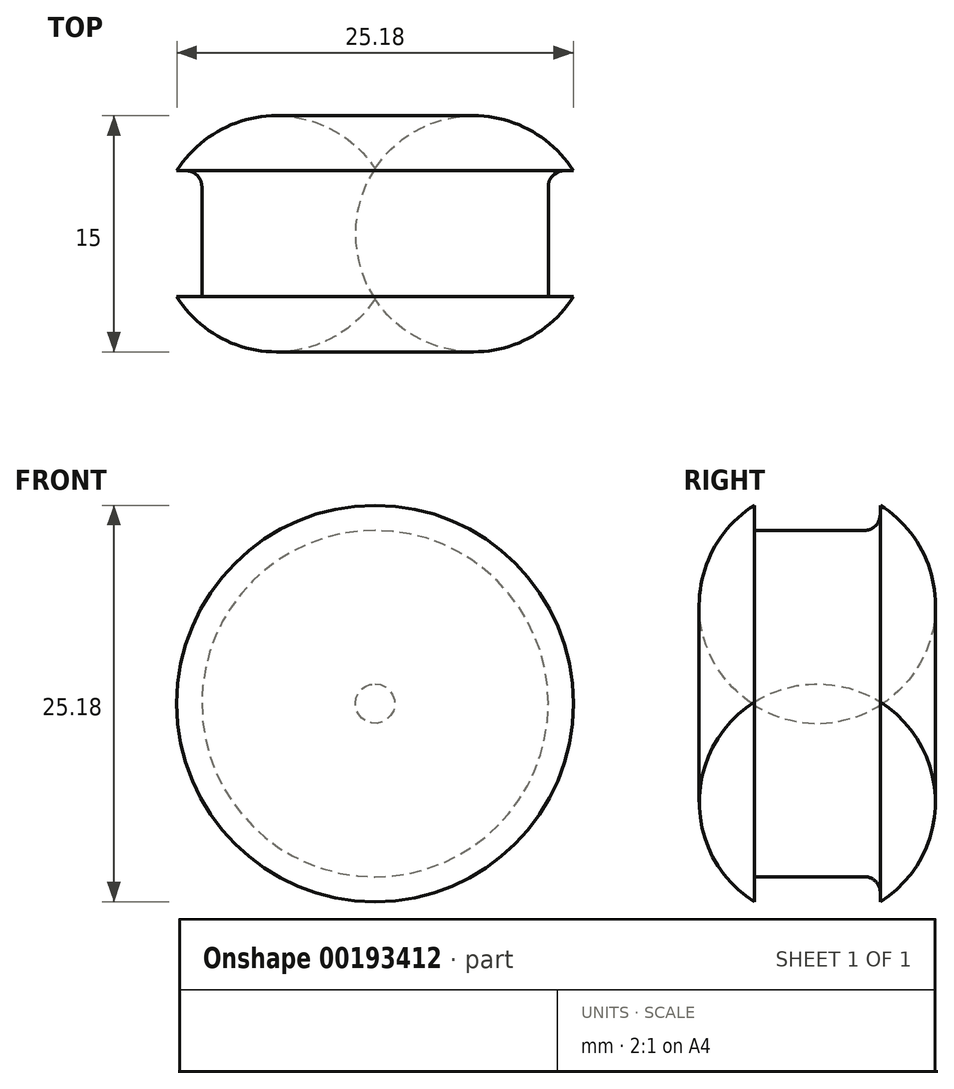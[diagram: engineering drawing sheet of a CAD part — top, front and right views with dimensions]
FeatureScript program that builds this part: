
annotation { "Feature Type Name" : "Feature", "Feature Type Description" : "" }
export const myFeature = defineFeature(function(context is Context, id is Id, definition is map)
    precondition{}
    {
        {
            var Q0;
            Q0=qCreatedBy(makeId("Right.planeOp"),FACE);
            var sketch = newSketch(context, id + "F0", { "sketchPlane" : qUnion([Q0])});
            skLineSegment(sketch, "E0", {"start": v(-28.73, 0) * mm, "end": v(29.21, 0) * mm, "construction": true});
            skLineSegment(sketch, "E1", {"start": v(-4, 11) * mm, "end": v(4, 11) * mm});
            skLineSegment(sketch, "E2", {"start": v(-4, 12.6) * mm, "end": v(5.31, 12.6) * mm, "construction": true});
            skLineSegment(sketch, "E3", {"start": v(-4, 11) * mm, "end": v(-4, 15.79) * mm});
            skLineSegment(sketch, "E4", {"start": v(4, 11) * mm, "end": v(4, 15.7) * mm});
            skArc(sketch, "E5", {"start": v(4, 12.6) * mm, "mid": v(0, 13.75) * mm, "end": v(-4, 12.6) * mm});
            skLineSegment(sketch, "E6.bottom", {"start": v(-4, 11) * mm, "end": v(-3, 11) * mm});
            skLineSegment(sketch, "E6.top", {"start": v(-4, 8) * mm, "end": v(-3, 8) * mm});
            skLineSegment(sketch, "E6.left", {"start": v(-4, 11) * mm, "end": v(-4, 8) * mm});
            skLineSegment(sketch, "E6.right", {"start": v(-3, 11) * mm, "end": v(-3, 8) * mm});
            skLineSegment(sketch, "E7", {"start": v(-3, 13.12) * mm, "end": v(3, 13.12) * mm, "construction": true});
            skSolve(sketch);
        }
        {
            var Q0;
            {var subQ2=sQuery(id+"F0.wireOp",EDGE,"E1");Q0=makeQuery(id+"F0.imprint","IMPRINT",FACE,{"disambiguationData":[TD([[makeQuery(id+"F0.imprint","IMPRINT",EDGE,{"derivedFrom":subQ2}),1.0]])]});}
            var Q1;
            Q1=makeQuery(id+"F0.imprint","IMPRINT",FACE,{"disambiguationData":[TD([[makeQuery(id+"F0.imprint","IMPRINT",EDGE,{"derivedFrom":sQuery(id+"F0.wireOp",EDGE,"E6.bottom")}),-1.0]])]});
            var Q2;
            Q2=sQuery(id+"F0.wireOp",EDGE,"E0");
            revolve(context, id + "F1", {"entities" : qUnion([Q0, Q1]), "axis" : qUnion([Q2]), "revolveType" : RevolveType.FULL});
        }
        {
            var Q0;
            Q0=makeQuery(id+"F1.opRevolve","SWEPT_EDGE",EDGE,{"disambiguationData":[OSD([sQuery(id+"F0.wireOp",EDGE,"E1"),sQuery(id+"F0.wireOp",EDGE,"E6.bottom"),sQuery(id+"F0.wireOp",EDGE,"E6.right")])]});
            fillet(context, id + "F2", {"entities" : qUnion([Q0]), "radius" : 1 * mm, "tangentPropagation" : true, "allowEdgeOverflow" : false});
        }
    });
